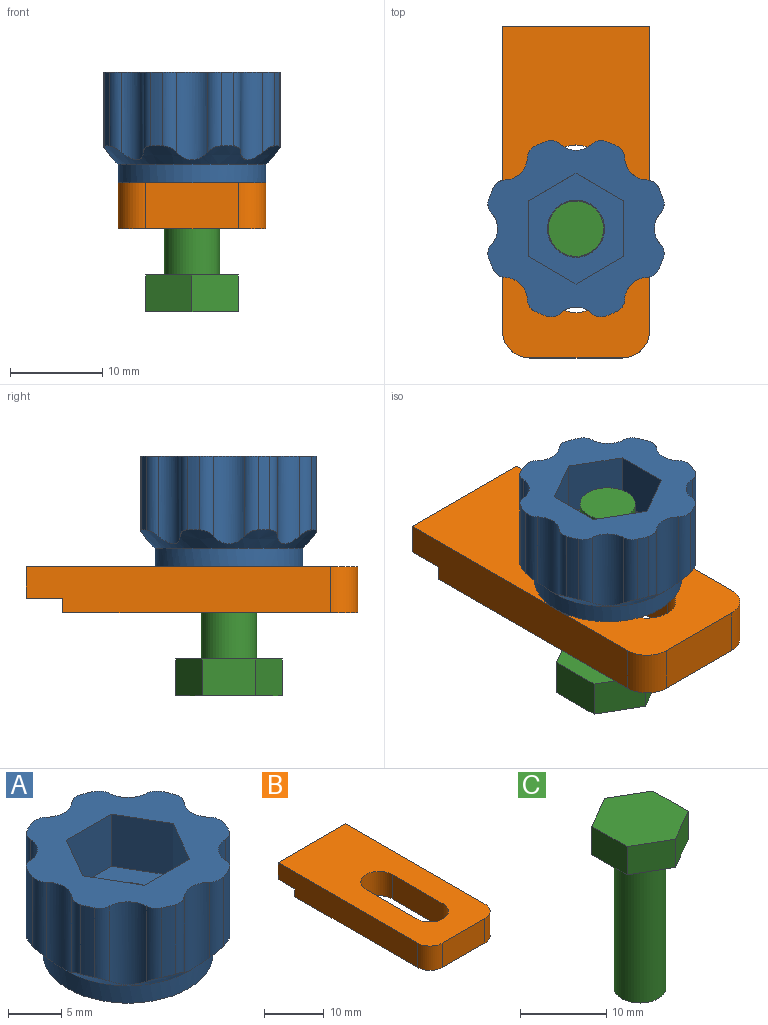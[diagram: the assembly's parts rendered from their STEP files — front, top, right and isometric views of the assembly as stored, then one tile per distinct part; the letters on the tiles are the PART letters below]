
ASSEMBLY  parts=3 mates=2
PART A: 44 faces, bbox 20x20x12 mm
  f0: cylinder r=10mm len=8mm, axis (0,0,-1), area 10.9mm2, adj f16,f26,f29,f43
  f1: cylinder r=2.5mm len=9.5mm, axis (0,0,1), area 34.3mm2, adj f16,f26,f28,f29
  f2: cylinder r=10mm len=8mm, axis (0,0,-1), area 10.9mm2, adj f16,f26,f28,f31
  f3: cylinder r=2.5mm len=9.5mm, axis (0,0,1), area 34.3mm2, adj f16,f26,f30,f31
  f4: cylinder r=10mm len=8mm, axis (0,0,-1), area 10.9mm2, adj f16,f26,f30,f33
  f5: cylinder r=2.5mm len=9.5mm, axis (0,0,1), area 34.3mm2, adj f16,f26,f32,f33
  f6: cylinder r=10mm len=8mm, axis (0,0,-1), area 10.9mm2, adj f16,f26,f32,f35
  f7: cylinder r=2.5mm len=9.5mm, axis (0,0,1), area 34.3mm2, adj f16,f26,f34,f35
  f8: cylinder r=10mm len=8mm, axis (0,0,-1), area 10.9mm2, adj f16,f26,f34,f37
  f9: cylinder r=2.5mm len=9.5mm, axis (0,0,1), area 34.3mm2, adj f16,f26,f36,f37
  f10: cylinder r=10mm len=8mm, axis (0,0,-1), area 10.9mm2, adj f16,f26,f36,f39
  f11: cylinder r=2.5mm len=9.5mm, axis (0,0,1), area 34.3mm2, adj f16,f26,f38,f39
  f12: cylinder r=10mm len=8mm, axis (0,0,-1), area 10.9mm2, adj f16,f26,f38,f41
  f13: cylinder r=2.5mm len=9.5mm, axis (0,0,1), area 34.3mm2, adj f16,f26,f40,f41
  f14: cylinder r=3.1mm len=6.2mm, axis (0,0,1), area 116.9mm2, adj f18,f25
  f15: cylinder r=10mm len=8mm, axis (0,0,-1), area 10.9mm2, adj f16,f26,f40,f42
  f16: plane 19.11x19.11mm, normal (0,0,1), area 181.4mm2, adj f0,f1,f2,f3,f4,f5,f6,f7
  f17: cylinder r=8mm len=16mm, axis (0,0,1), area 100.5mm2, adj f18,f26
  f18: plane 16x16mm, normal (0,0,-1), area 170.9mm2, adj f14,f17
  f19: plane 6x5.2mm, normal (0.87,0.5,0), area 36mm2, adj f16,f20,f24,f25
  f20: plane 6x6mm, normal (0,1,0), area 36mm2, adj f16,f19,f21,f25
  f21: plane 6x5.2mm, normal (-0.87,0.5,0), area 36mm2, adj f16,f20,f22,f25
  f22: plane 6x5.2mm, normal (-0.87,-0.5,0), area 36mm2, adj f16,f21,f23,f25
  f23: plane 6x6mm, normal (0,-1,0), area 36mm2, adj f16,f22,f24,f25
  f24: plane 6x5.2mm, normal (0.87,-0.5,0), area 36mm2, adj f16,f19,f23,f25
  f25: plane 12.01x10.4mm, normal (0,0,1), area 63.5mm2, adj f14,f19,f20,f21,f22,f23,f24
  f26: cone r=8mm half-angle=45deg, axis (0,0,1), area 104.7mm2, adj f0,f1,f2,f3,f4,f5,f6,f7
  f27: cylinder r=2.5mm len=9.5mm, axis (0,0,1), area 34.3mm2, adj f16,f26,f42,f43
  f28: cylinder r=1.5mm len=8.68mm, axis (0,0,-1), area 13.2mm2, adj f1,f2,f16,f26
  f29: cylinder r=1.5mm len=8.68mm, axis (0,0,-1), area 13.2mm2, adj f0,f1,f16,f26
  f30: cylinder r=1.5mm len=8.68mm, axis (0,0,-1), area 13.2mm2, adj f3,f4,f16,f26
  f31: cylinder r=1.5mm len=8.68mm, axis (0,0,-1), area 13.2mm2, adj f2,f3,f16,f26
  f32: cylinder r=1.5mm len=8.68mm, axis (0,0,-1), area 13.2mm2, adj f5,f6,f16,f26
  f33: cylinder r=1.5mm len=8.68mm, axis (0,0,-1), area 13.2mm2, adj f4,f5,f16,f26
  f34: cylinder r=1.5mm len=8.68mm, axis (0,0,-1), area 13.2mm2, adj f7,f8,f16,f26
  f35: cylinder r=1.5mm len=8.68mm, axis (0,0,-1), area 13.2mm2, adj f6,f7,f16,f26
  f36: cylinder r=1.5mm len=8.68mm, axis (0,0,-1), area 13.2mm2, adj f9,f10,f16,f26
  f37: cylinder r=1.5mm len=8.68mm, axis (0,0,-1), area 13.2mm2, adj f8,f9,f16,f26
  f38: cylinder r=1.5mm len=8.68mm, axis (0,0,-1), area 13.2mm2, adj f11,f12,f16,f26
  f39: cylinder r=1.5mm len=8.68mm, axis (0,0,-1), area 13.2mm2, adj f10,f11,f16,f26
  f40: cylinder r=1.5mm len=8.68mm, axis (0,0,-1), area 13.2mm2, adj f13,f15,f16,f26
  f41: cylinder r=1.5mm len=8.68mm, axis (0,0,-1), area 13.2mm2, adj f12,f13,f16,f26
  f42: cylinder r=1.5mm len=8.68mm, axis (0,0,-1), area 13.2mm2, adj f15,f16,f26,f27
  f43: cylinder r=1.5mm len=8.68mm, axis (0,0,-1), area 13.2mm2, adj f0,f16,f26,f27
PART B: 14 faces, bbox 16x36x5 mm
  f0: plane 33x5mm, normal (-1,0,0), area 158.6mm2, adj f3,f8,f9,f10,f11,f13
  f1: plane 10x5mm, normal (0,-1,0), area 50mm2, adj f8,f9,f12,f13
  f2: plane 33x5mm, normal (1,0,0), area 158.6mm2, adj f3,f8,f9,f10,f11,f12
  f3: plane 16x3.4mm, normal (0,1,0), area 54.4mm2, adj f0,f2,f8,f11
  f4: cylinder r=3.1mm len=6.2mm, axis (0,0,-1), area 48.7mm2, adj f5,f7,f8,f9
  f5: plane 12x5mm, normal (-1,0,0), area 60mm2, adj f4,f6,f8,f9
  f6: cylinder r=3.1mm len=6.2mm, axis (0,0,-1), area 48.7mm2, adj f5,f7,f8,f9
  f7: plane 12x5mm, normal (1,0,0), area 60mm2, adj f4,f6,f8,f9
  f8: plane 36x16mm, normal (0,0,1), area 467.5mm2, adj f0,f1,f2,f3,f4,f5,f6,f7
  f9: plane 32x16mm, normal (0,0,-1), area 403.5mm2, adj f0,f1,f2,f4,f5,f6,f7,f10
  f10: plane 16x1.6mm, normal (0,1,0), area 25.6mm2, adj f0,f2,f9,f11
  f11: plane 16x4mm, normal (0,0,-1), area 64mm2, adj f0,f2,f3,f10
  f12: cylinder r=3mm len=5mm, axis (0,0,1), area 23.6mm2, adj f1,f2,f8,f9
  f13: cylinder r=3mm len=5mm, axis (0,0,-1), area 23.6mm2, adj f0,f1,f8,f9
PART C: 10 faces, bbox 10x11.5x24 mm
  f0: cylinder r=3mm len=20mm, axis (0,0,-1), area 377mm2, adj f1,f9
  f1: plane 6x6mm, normal (0,0,-1), area 28.3mm2, adj f0
  f2: plane 5x4mm, normal (0.5,-0.87,0), area 23.1mm2, adj f3,f7,f8,f9
  f3: plane 5.77x4mm, normal (1,0,0), area 23.1mm2, adj f2,f4,f8,f9
  f4: plane 5x4mm, normal (0.5,0.87,0), area 23.1mm2, adj f3,f5,f8,f9
  f5: plane 5x4mm, normal (-0.5,0.87,0), area 23.1mm2, adj f4,f6,f8,f9
  f6: plane 5.77x4mm, normal (-1,0,0), area 23.1mm2, adj f5,f7,f8,f9
  f7: plane 5x4mm, normal (-0.5,-0.87,0), area 23.1mm2, adj f2,f6,f8,f9
  f8: plane 11.55x10mm, normal (0,0,1), area 86.6mm2, adj f2,f3,f4,f5,f6,f7
  f9: plane 11.55x10mm, normal (0,0,-1), area 58.3mm2, adj f0,f2,f3,f4,f5,f6,f7
PLACE A rot(axis=(0,0,-1),90deg) t=(7.77,-4.44,4.38)mm
PLACE B t=(7.77,-0.44,-4.62)mm
PLACE C rot(axis=(0,-1,0),180deg) t=(7.77,-4.44,10.38)mm
MATE fastened A.f17 <-> B.f8  axis (0,0,-1) through (7.77,-4.44,0.38)mm
MATE fastened A.f14 <-> C.f0  axis (0,0,1) through (7.77,-4.44,0.38)mm
